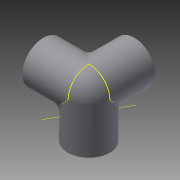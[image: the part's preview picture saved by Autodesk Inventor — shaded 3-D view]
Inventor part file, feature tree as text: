
AUTODESK INVENTOR PART (.ipt)
format: ipt  version: 2015 SP1 (Build 190203100, 203)  size: 325,632 bytes
history: native  units: mm
features: sketch x8, projected_geometry x8, other x5, extrude x5, pattern_circular x2, fillet x1, revolve x1
ambient origin geometry x8: Origin, YZ Plane, XZ Plane, XY Plane, X Axis, Y Axis, Z Axis, Center Point
bodies: Body1 (feature_tree)
feature tree (30):
  other  "Sólido1"
  extrude  "Extrusión1"  Depth=12.0mm
  extrude  "Extrusión2"  Depth=6.0mm TaperAngle=0.0deg
  other  "Eje de trabajo1"
  other  "Eje de trabajo2"
  pattern_circular  "Patrón circular3"  Count=2 Angle=90.0deg
  other  "Eje de trabajo6"
  pattern_circular  "Patrón circular5"  Count=2 Angle=90.0deg
  fillet  "Empalme4"  Radius=2.0mm
  extrude  "Extrusión13"  Depth=10.0mm TaperAngle=0.0deg
  extrude  "Extrusión14"  TaperAngle=90.0deg  [1 undecoded]
  extrude  "Extrusión15"  [1 undecoded]
  sketch  "Boceto17"
  sketch  "Boceto18"
  sketch  "Boceto19"
  revolve  "Revolución1"  [1 undecoded]
  sketch  "Boceto1"  dims[d0=8.0mm d1=12.0mm]
  sketch  "Boceto2"  dims[d2=7.0mm d3=0.0mm d4=6.0mm d5=0.0mm d19=20.0mm d20=90.0deg d41=20.0mm d42=90.0deg d44=2.0mm]
  other  "Punto de trabajo1"
  sketch  "Boceto14"  dims[d45=10.0mm d46=0.0mm d47=10.0mm d48=0.0mm]
  projected_geometry  "Contorno proyectado12"
  sketch  "Boceto15"  dims[d49=10.0mm d50=0.0mm d51=90.0deg]
  projected_geometry  "Contorno proyectado13"
  projected_geometry  "Contorno proyectado14"
  projected_geometry  "Contorno proyectado15"
  sketch  "Boceto16"
  projected_geometry  "Contorno proyectado16"
  projected_geometry  "Contorno proyectado17"
  projected_geometry  "Contorno proyectado18"
  projected_geometry  "Contorno proyectado19"
note: 3 required parameter values undecoded (feature->parameter linkage not recoverable at this tier; creation-order binding heuristic only, values carry confidence <= 0.55)
